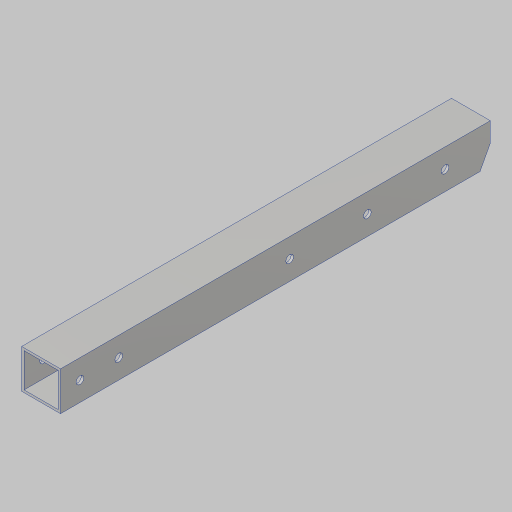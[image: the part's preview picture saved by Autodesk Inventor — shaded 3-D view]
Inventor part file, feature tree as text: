
AUTODESK INVENTOR PART (.ipt)
format: ipt  version: 2023.5 (Build 275446000, 446)  size: 214,528 bytes
history: native  units: in
note: dims shown in document units (in); Inventor stores cm internally (conversion verified against a paired STEP export)
features: sketch x3, extrude x2, hole x2, projected_geometry x2
ambient origin geometry x8: Origin, YZ Plane, XZ Plane, XY Plane, X Axis, Y Axis, Z Axis, Center Point
bodies: Solid1 (feature_tree)
feature tree (9):
  extrude  "Extrusion1"  Depth=1.0in
  hole  "Hole1"  [1 undecoded]
  extrude  "Extrusion2"  Depth=1.0in TaperAngle=0.0deg
  hole  "Hole2"  [1 undecoded]
  sketch  "Sketch2"  dims[d4=0.0in d5=1.0in]
  sketch  "Sketch3"  dims[d6=0.5in]
  projected_geometry  "Projected Loop1"
  sketch  "Sketch4"  dims[d7=0.201in d8=0.75in d9=0.385in d10=0.25in d11=0.5635in d12=1.0in d13=0.8108in d14=0.1924in d15=1.0in d16=0.0in d19=2.0in d20=2.0in d21=1.1673in d22=0.5001in d23=0.201in d24=0.75in d25=0.385in d26=0.25in d27=0.5635in d28=1.0in d29=0.8108in]
  projected_geometry  "Project Cut Edges1"
note: 2 required parameter values undecoded (feature->parameter linkage not recoverable at this tier; creation-order binding heuristic only, values carry confidence <= 0.55)
